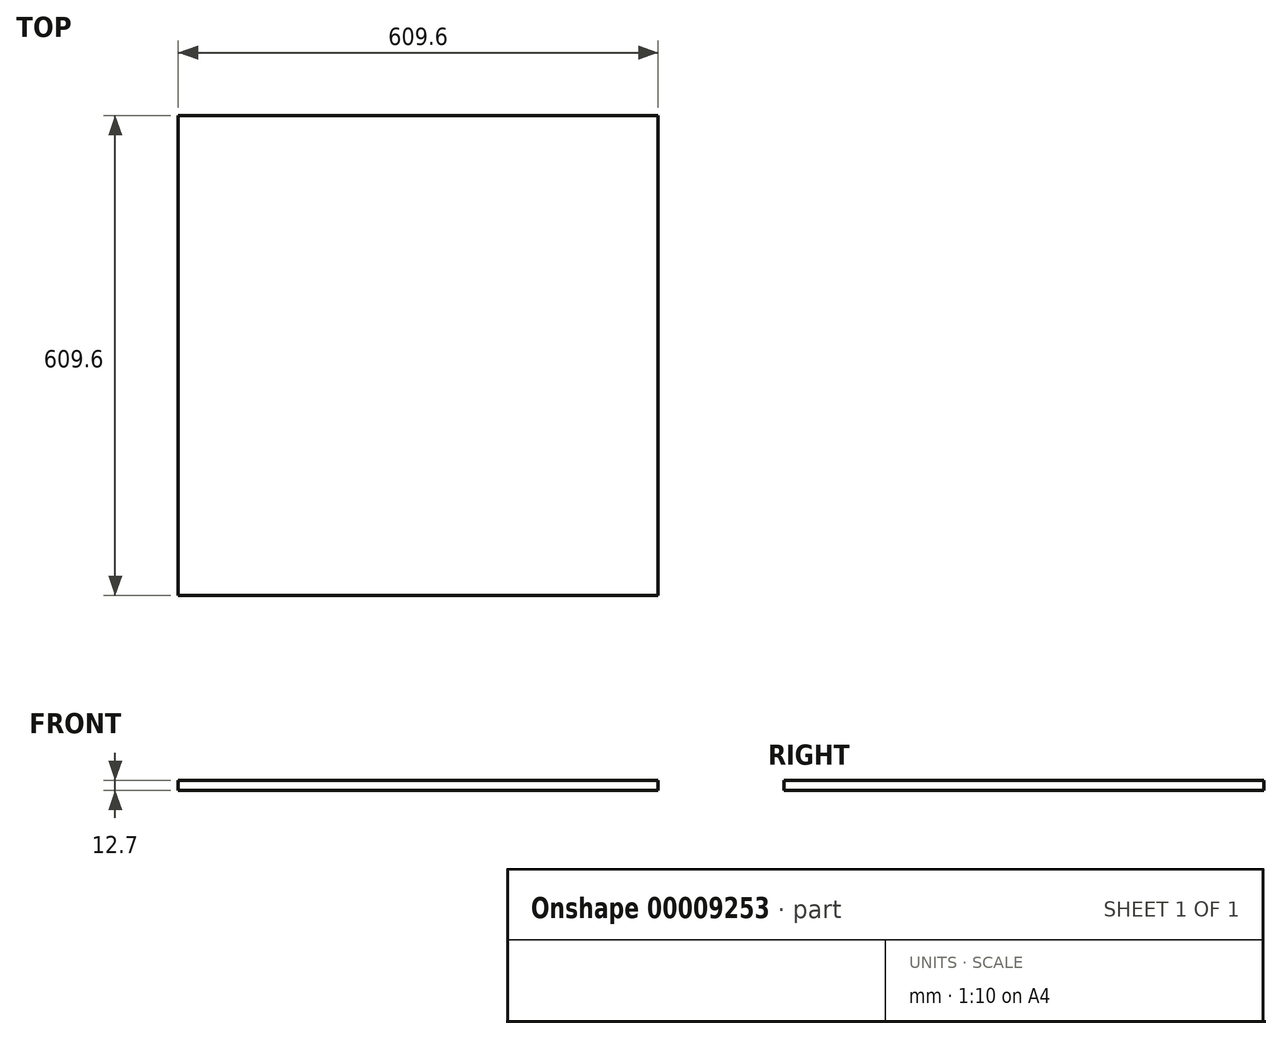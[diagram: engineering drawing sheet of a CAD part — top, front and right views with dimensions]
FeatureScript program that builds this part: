
annotation { "Feature Type Name" : "Feature", "Feature Type Description" : "" }
export const myFeature = defineFeature(function(context is Context, id is Id, definition is map)
    precondition{}
    {
        {
            var Q0;
            Q0=qCreatedBy(makeId("Top.planeOp"),FACE);
            var sketch = newSketch(context, id + "F0", { "sketchPlane" : qUnion([Q0])});
            skLineSegment(sketch, "E0.rect.bottom", {"start": v(304.8, 304.8) * mm, "end": v(-304.8, 304.8) * mm});
            skLineSegment(sketch, "E0.rect.top", {"start": v(304.8, -304.8) * mm, "end": v(-304.8, -304.8) * mm});
            skLineSegment(sketch, "E0.rect.left", {"start": v(304.8, 304.8) * mm, "end": v(304.8, -304.8) * mm});
            skLineSegment(sketch, "E0.rect.right", {"start": v(-304.8, 304.8) * mm, "end": v(-304.8, -304.8) * mm});
            skPoint(sketch, "E0.rect.middle", {"position": v(0, 0) * mm});
            skSolve(sketch);
        }
        {
            var Q0;
            Q0=makeQuery(id+"F0.imprint","IMPRINT",FACE,{"disambiguationData":[TD([[makeQuery(id+"F0.imprint","IMPRINT",EDGE,{"derivedFrom":sQuery(id+"F0.wireOp",EDGE,"E0.rect.bottom")}),1.0]])]});
            extrude(context, id + "F1", {"entities" : qUnion([Q0]), "depth" : 12.7 * mm});
        }
    });
